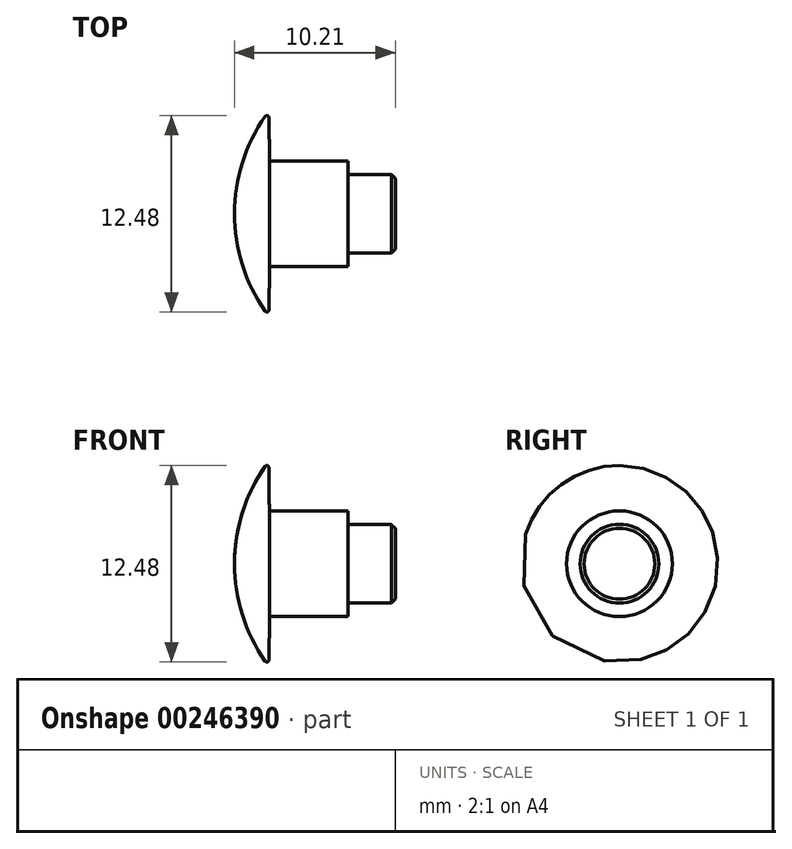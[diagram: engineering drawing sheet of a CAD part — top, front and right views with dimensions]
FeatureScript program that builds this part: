
annotation { "Feature Type Name" : "Feature", "Feature Type Description" : "" }
export const myFeature = defineFeature(function(context is Context, id is Id, definition is map)
    precondition{}
    {
        {
            var Q0;
            Q0=qCreatedBy(makeId("Front.planeOp"),FACE);
            var sketch = newSketch(context, id + "F0", { "sketchPlane" : qUnion([Q0])});
            skLineSegment(sketch, "E0", {"start": v(0, 0) * mm, "end": v(10.21, 0) * mm});
            skLineSegment(sketch, "E1", {"start": v(10.21, 0) * mm, "end": v(10.21, 2.5) * mm});
            skLineSegment(sketch, "E2", {"start": v(10.21, 2.5) * mm, "end": v(7.21, 2.5) * mm});
            skLineSegment(sketch, "E3", {"start": v(7.21, 3.36) * mm, "end": v(7.21, 2.5) * mm});
            skLineSegment(sketch, "E4", {"start": v(7.21, 3.36) * mm, "end": v(2.21, 3.36) * mm});
            skLineSegment(sketch, "E5", {"start": v(2.21, 3.36) * mm, "end": v(2.21, 3.36) * mm});
            skLineSegment(sketch, "E6", {"start": v(2.17, 6.5) * mm, "end": v(2.17, 6.5) * mm});
            skLineSegment(sketch, "E7", {"start": v(2.17, 6.5) * mm, "end": v(2.21, 3.36) * mm});
            skArc(sketch, "E8", {"start": v(2.17, 6.5) * mm, "mid": v(0.56, 3.43) * mm, "end": v(0, 0) * mm});
            skSolve(sketch);
        }
        {
            var Q0;
            Q0=makeQuery(id+"F0.imprint","IMPRINT",FACE,{"disambiguationData":[TD([[makeQuery(id+"F0.imprint","IMPRINT",EDGE,{"derivedFrom":sQuery(id+"F0.wireOp",EDGE,"E0")}),1.0]])]});
            var Q1;
            Q1=sQuery(id+"F0.wireOp",EDGE,"E0");
            revolve(context, id + "F1", {"entities" : qUnion([Q0]), "axis" : qUnion([Q1]), "revolveType" : RevolveType.FULL});
        }
        {
            var Q0;
            Q0=makeQuery(id+"F1.opRevolve","SWEPT_EDGE",EDGE,{"disambiguationData":[OSD([sQuery(id+"F0.wireOp",EDGE,"E1"),sQuery(id+"F0.wireOp",EDGE,"E2")])]});
            chamfer(context, id + "F2", {"entities" : qUnion([Q0]), "width" : 0.25 * mm, "tangentPropagation" : true});
        }
        {
            var Q0;
            Q0=makeQuery(id+"F1.opRevolve","SWEPT_EDGE",EDGE,{"disambiguationData":[OSD([sQuery(id+"F0.wireOp",EDGE,"E7"),sQuery(id+"F0.wireOp",EDGE,"E8")])]});
            fillet(context, id + "F3", {"entities" : qUnion([Q0]), "radius" : 0.13 * mm, "tangentPropagation" : true, "allowEdgeOverflow" : false});
        }
    });
